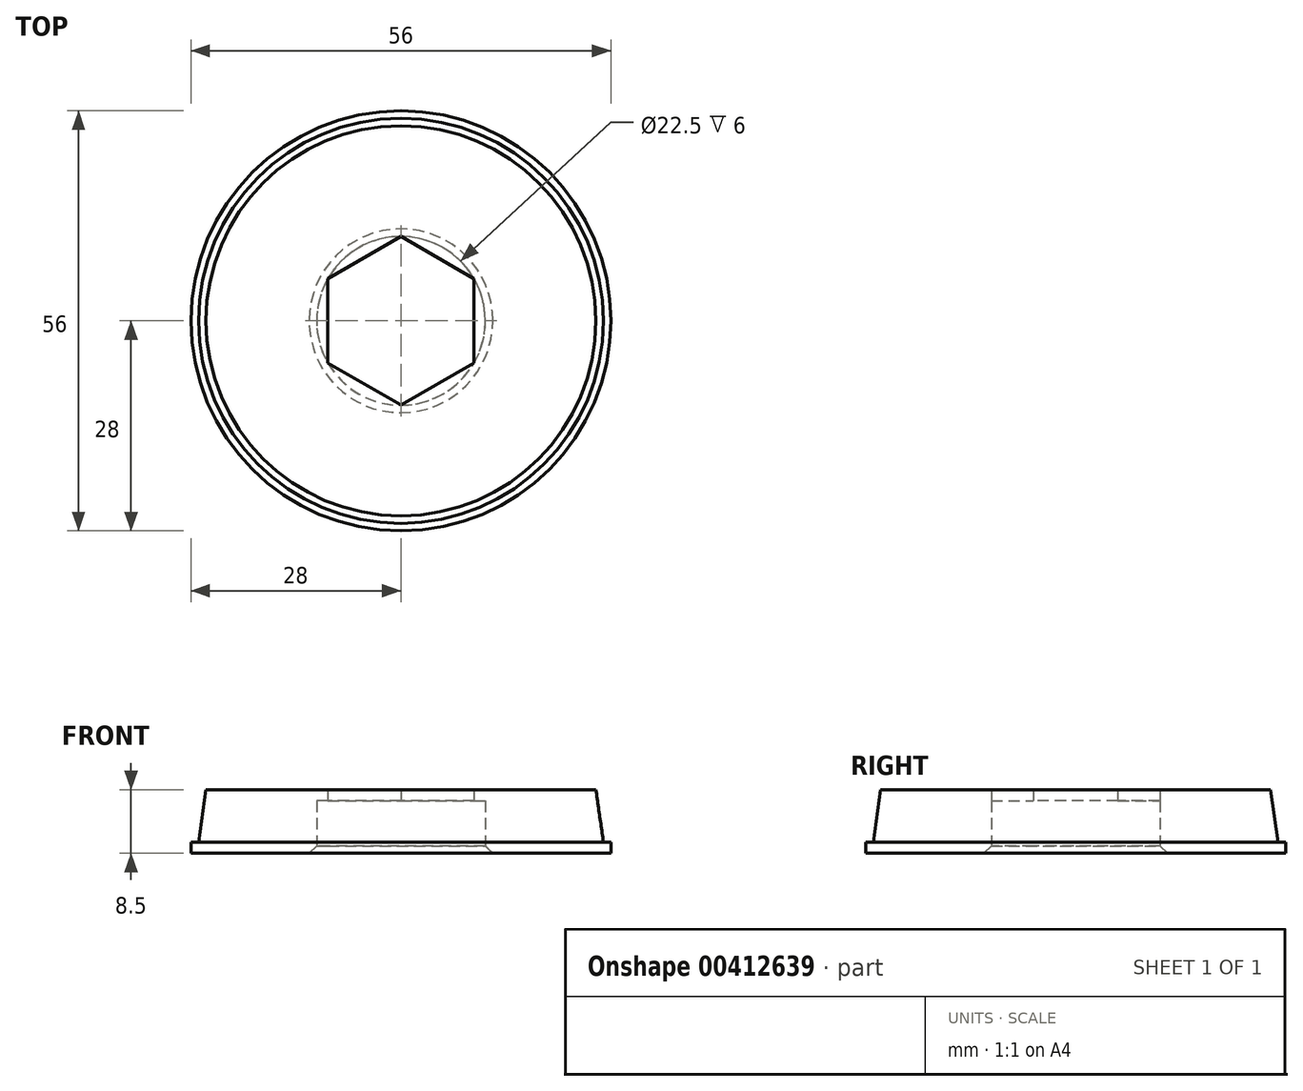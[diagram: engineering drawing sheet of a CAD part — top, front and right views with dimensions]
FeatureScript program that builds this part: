
annotation { "Feature Type Name" : "Feature", "Feature Type Description" : "" }
export const myFeature = defineFeature(function(context is Context, id is Id, definition is map)
    precondition{}
    {
        {
            assignVariable(context, id + "F0", {"name" : "BEARING_HEIGHT", "anyValue" : 7});
        }
        {
            assignVariable(context, id + "F1", {"name" : "UPPER_TICKNESS", "anyValue" : 1.5});
        }
        {
            assignVariable(context, id + "F2", {"name" : "LOWER_TICKNESS", "anyValue" : 1.5});
        }
        {
            assignVariable(context, id + "F3", {"name" : "EASY_MOUNT_CHAMFER_THING", "anyValue" : 1});
        }
        {
            assignVariable(context, id + "F4", {"name" : "BEARING_CHAMFER", "anyValue" : 1});
        }
        {
            var Q0;
            Q0=qCreatedBy(makeId("Top.planeOp"),FACE);
            var sketch = newSketch(context, id + "F5", { "sketchPlane" : qUnion([Q0])});
            skCircle(sketch, "E0", {"center": v(0, 0) * mm, "radius": 27 * mm});
            skCircle(sketch, "E1", {"center": v(0, 0) * mm, "radius": 11.25 * mm});
            skCircle(sketch, "E2", {"center": v(0, 0) * mm, "radius": 28 * mm});
            skCircle(sketch, "E3.cCircle", {"center": v(0, 0) * mm, "radius": 9.74 * mm, "construction": true});
            skLineSegment(sketch, "E3.0", {"start": v(9.74, 5.62) * mm, "end": v(9.74, -5.62) * mm});
            skLineSegment(sketch, "E3.1", {"start": v(9.74, -5.63) * mm, "end": v(0, -11.25) * mm});
            skLineSegment(sketch, "E3.2", {"start": v(0, -11.25) * mm, "end": v(-9.74, -5.62) * mm});
            skLineSegment(sketch, "E3.3", {"start": v(-9.74, -5.62) * mm, "end": v(-9.74, 5.62) * mm});
            skLineSegment(sketch, "E3.4", {"start": v(-9.74, 5.63) * mm, "end": v(0, 11.25) * mm});
            skLineSegment(sketch, "E3.5", {"start": v(0, 11.25) * mm, "end": v(9.74, 5.62) * mm});
            skPoint(sketch, "E3.0.midPoint", {"position": v(9.74, 0) * mm});
            skSolve(sketch);
        }
        {
            var Q0;
            Q0=makeQuery(id+"F5.imprint","IMPRINT",FACE,{"disambiguationData":[TD([[makeQuery(id+"F5.imprint","IMPRINT",EDGE,{"derivedFrom":sQuery(id+"F5.wireOp",EDGE,"E0")}),1.0]])]});
            var Q1;
            {var subQ0=sQuery(id+"F5.wireOp",EDGE,"E3.3");Q1=makeQuery(id+"F5.imprint","IMPRINT",FACE,{"disambiguationData":[TD([[makeQuery(id+"F5.imprint","IMPRINT",EDGE,{"derivedFrom":subQ0}),1.0]])]});}
            var Q2;
            {var subQ0=sQuery(id+"F5.wireOp",EDGE,"E3.5");Q2=makeQuery(id+"F5.imprint","IMPRINT",FACE,{"disambiguationData":[TD([[makeQuery(id+"F5.imprint","IMPRINT",EDGE,{"derivedFrom":subQ0}),1.0]])]});}
            var Q3;
            {var subQ0=sQuery(id+"F5.wireOp",EDGE,"E3.0");Q3=makeQuery(id+"F5.imprint","IMPRINT",FACE,{"disambiguationData":[TD([[makeQuery(id+"F5.imprint","IMPRINT",EDGE,{"derivedFrom":subQ0}),1.0]])]});}
            var Q4;
            {var subQ0=sQuery(id+"F5.wireOp",EDGE,"E3.1");Q4=makeQuery(id+"F5.imprint","IMPRINT",FACE,{"disambiguationData":[TD([[makeQuery(id+"F5.imprint","IMPRINT",EDGE,{"derivedFrom":subQ0}),1.0]])]});}
            var Q5;
            {var subQ0=sQuery(id+"F5.wireOp",EDGE,"E3.2");Q5=makeQuery(id+"F5.imprint","IMPRINT",FACE,{"disambiguationData":[TD([[makeQuery(id+"F5.imprint","IMPRINT",EDGE,{"derivedFrom":subQ0}),1.0]])]});}
            var Q6;
            {var subQ0=sQuery(id+"F5.wireOp",EDGE,"E3.4");Q6=makeQuery(id+"F5.imprint","IMPRINT",FACE,{"disambiguationData":[TD([[makeQuery(id+"F5.imprint","IMPRINT",EDGE,{"derivedFrom":subQ0}),1.0]])]});}
            var Q7;
            Q7=makeQuery(id+"F5.imprint","IMPRINT",FACE,{"disambiguationData":[TD([[makeQuery(id+"F5.imprint","IMPRINT",EDGE,{"derivedFrom":sQuery(id+"F5.wireOp",EDGE,"E3.0")}),-1.0]])]});
            extrude(context, id + "F6", {"entities" : qUnion([Q0, Q1, Q2, Q3, Q4, Q5, Q6, Q7]), "depth" : (getVariable(context, 'BEARING_HEIGHT') + getVariable(context, 'UPPER_TICKNESS') - getVariable(context, 'LOWER_TICKNESS')) * mm, "hasSecondDirectionDraft" : true, "secondDirectionDraftAngle" : 3 * degree});
        }
        {
            var Q0;
            Q0=makeQuery(id+"F5.imprint","IMPRINT",FACE,{"disambiguationData":[TD([[makeQuery(id+"F5.imprint","IMPRINT",EDGE,{"derivedFrom":sQuery(id+"F5.wireOp",EDGE,"E3.0")}),-1.0]])]});
            var Q1;
            Q1=makeQuery(id+"F5.imprint","IMPRINT",FACE,{"disambiguationData":[TD([[makeQuery(id+"F5.imprint","IMPRINT",EDGE,{"derivedFrom":sQuery(id+"F5.wireOp",EDGE,"E0")}),1.0]])]});
            var Q2;
            {var subQ0=sQuery(id+"F5.wireOp",EDGE,"E3.0");Q2=makeQuery(id+"F5.imprint","IMPRINT",FACE,{"disambiguationData":[TD([[makeQuery(id+"F5.imprint","IMPRINT",EDGE,{"derivedFrom":subQ0}),1.0]])]});}
            var Q3;
            {var subQ0=sQuery(id+"F5.wireOp",EDGE,"E3.1");Q3=makeQuery(id+"F5.imprint","IMPRINT",FACE,{"disambiguationData":[TD([[makeQuery(id+"F5.imprint","IMPRINT",EDGE,{"derivedFrom":subQ0}),1.0]])]});}
            var Q4;
            {var subQ0=sQuery(id+"F5.wireOp",EDGE,"E3.2");Q4=makeQuery(id+"F5.imprint","IMPRINT",FACE,{"disambiguationData":[TD([[makeQuery(id+"F5.imprint","IMPRINT",EDGE,{"derivedFrom":subQ0}),1.0]])]});}
            var Q5;
            {var subQ0=sQuery(id+"F5.wireOp",EDGE,"E3.3");Q5=makeQuery(id+"F5.imprint","IMPRINT",FACE,{"disambiguationData":[TD([[makeQuery(id+"F5.imprint","IMPRINT",EDGE,{"derivedFrom":subQ0}),1.0]])]});}
            var Q6;
            {var subQ0=sQuery(id+"F5.wireOp",EDGE,"E3.5");Q6=makeQuery(id+"F5.imprint","IMPRINT",FACE,{"disambiguationData":[TD([[makeQuery(id+"F5.imprint","IMPRINT",EDGE,{"derivedFrom":subQ0}),1.0]])]});}
            var Q7;
            {var subQ0=sQuery(id+"F5.wireOp",EDGE,"E3.4");Q7=makeQuery(id+"F5.imprint","IMPRINT",FACE,{"disambiguationData":[TD([[makeQuery(id+"F5.imprint","IMPRINT",EDGE,{"derivedFrom":subQ0}),1.0]])]});}
            var Q8;
            Q8=makeQuery(id+"F5.imprint","IMPRINT",FACE,{"disambiguationData":[TD([[makeQuery(id+"F5.imprint","IMPRINT",EDGE,{"derivedFrom":sQuery(id+"F5.wireOp",EDGE,"E0")}),-1.0]])]});
            extrude(context, id + "F7", {"entities" : qUnion([Q0, Q1, Q2, Q3, Q4, Q5, Q6, Q7, Q8]), "operationType" : NewBodyOperationType.ADD, "oppositeDirection" : true, "depth" : getVariable(context, 'LOWER_TICKNESS') * mm});
        }
        {
            var Q0;
            Q0=makeQuery(id+"F5.imprint","IMPRINT",FACE,{"disambiguationData":[TD([[makeQuery(id+"F5.imprint","IMPRINT",EDGE,{"derivedFrom":sQuery(id+"F5.wireOp",EDGE,"E3.0")}),-1.0]])]});
            var Q1;
            Q1=makeQuery(id+"F6.opExtrude","CAP_FACE",FACE,{"disambiguationData":[OSD([sQuery(id+"F5.wireOp",EDGE,"E0"),sQuery(id+"F5.wireOp",EDGE,"E1")])],"isStart":false});
            extrude(context, id + "F8", {"entities" : qUnion([Q0]), "operationType" : NewBodyOperationType.REMOVE, "endBound" : BoundingType.THROUGH_ALL, "endBoundEntityFace" : qUnion([Q1]), "depth" : 25 * mm, "hasSecondDirection" : true, "secondDirectionBound" : SecondDirectionBoundingType.THROUGH_ALL, "secondDirectionOppositeDirection" : true, "secondDirectionDepth" : 2 * mm});
        }
        {
            var Q0;
            {var subQ0=sQuery(id+"F5.wireOp",EDGE,"E3.2");Q0=makeQuery(id+"F5.imprint","IMPRINT",FACE,{"disambiguationData":[TD([[makeQuery(id+"F5.imprint","IMPRINT",EDGE,{"derivedFrom":subQ0}),1.0]])]});}
            var Q1;
            {var subQ0=sQuery(id+"F5.wireOp",EDGE,"E3.1");Q1=makeQuery(id+"F5.imprint","IMPRINT",FACE,{"disambiguationData":[TD([[makeQuery(id+"F5.imprint","IMPRINT",EDGE,{"derivedFrom":subQ0}),1.0]])]});}
            var Q2;
            {var subQ0=sQuery(id+"F5.wireOp",EDGE,"E3.0");Q2=makeQuery(id+"F5.imprint","IMPRINT",FACE,{"disambiguationData":[TD([[makeQuery(id+"F5.imprint","IMPRINT",EDGE,{"derivedFrom":subQ0}),1.0]])]});}
            var Q3;
            {var subQ0=sQuery(id+"F5.wireOp",EDGE,"E3.5");Q3=makeQuery(id+"F5.imprint","IMPRINT",FACE,{"disambiguationData":[TD([[makeQuery(id+"F5.imprint","IMPRINT",EDGE,{"derivedFrom":subQ0}),1.0]])]});}
            var Q4;
            {var subQ0=sQuery(id+"F5.wireOp",EDGE,"E3.4");Q4=makeQuery(id+"F5.imprint","IMPRINT",FACE,{"disambiguationData":[TD([[makeQuery(id+"F5.imprint","IMPRINT",EDGE,{"derivedFrom":subQ0}),1.0]])]});}
            var Q5;
            {var subQ0=sQuery(id+"F5.wireOp",EDGE,"E3.3");Q5=makeQuery(id+"F5.imprint","IMPRINT",FACE,{"disambiguationData":[TD([[makeQuery(id+"F5.imprint","IMPRINT",EDGE,{"derivedFrom":subQ0}),1.0]])]});}
            extrude(context, id + "F9", {"entities" : qUnion([Q0, Q1, Q2, Q3, Q4, Q5]), "operationType" : NewBodyOperationType.REMOVE, "depth" : (getVariable(context, 'BEARING_HEIGHT') - getVariable(context, 'LOWER_TICKNESS')) * mm, "hasSecondDirection" : true, "secondDirectionBound" : SecondDirectionBoundingType.THROUGH_ALL, "secondDirectionOppositeDirection" : true, "secondDirectionDepth" : 2 * mm});
        }
        {
            var Q0;
            Q0=makeQuery(id+"F6.opExtrude","CAP_EDGE",EDGE,{"disambiguationData":[OSD([sQuery(id+"F5.wireOp",EDGE,"E0")])],"isStart":false});
            chamfer(context, id + "F10", {"entities" : qUnion([Q0]), "chamferType" : ChamferType.TWO_OFFSETS, "width1" : getVariable(context, 'BEARING_HEIGHT') * mm, "oppositeDirection" : true, "width2" : getVariable(context, 'EASY_MOUNT_CHAMFER_THING') * mm, "tangentPropagation" : true});
        }
        {
            var Q0;
            {var subQ0=sQuery(id+"F5.wireOp",EDGE,"E3.5");var subQ1=sQuery(id+"F5.wireOp",EDGE,"E3.0");var subQ2=sQuery(id+"F5.wireOp",EDGE,"E1");var subQ3=makeQuery(id+"F5.imprint","INTERSECT",VERTEX,{"derivedFrom":[subQ2,subQ1,subQ0]});var subQ4=sQuery(id+"F5.wireOp",EDGE,"E3.1");var subQ5=makeQuery(id+"F5.imprint","INTERSECT",VERTEX,{"derivedFrom":[subQ2,subQ1,subQ4]});var subQ6=sQuery(id+"F5.wireOp",EDGE,"E3.2");var subQ7=makeQuery(id+"F5.imprint","INTERSECT",VERTEX,{"derivedFrom":[subQ2,subQ4,subQ6]});var subQ8=sQuery(id+"F5.wireOp",EDGE,"E3.3");var subQ9=makeQuery(id+"F5.imprint","INTERSECT",VERTEX,{"derivedFrom":[subQ2,subQ6,subQ8]});var subQ10=sQuery(id+"F5.wireOp",EDGE,"E3.4");var subQ11=makeQuery(id+"F5.imprint","INTERSECT",VERTEX,{"derivedFrom":[subQ2,subQ8,subQ10]});Q0=makeQuery(id+"F9.boolean.opBoolean","INTERSECT",EDGE,{"derivedFrom":[makeQuery(id+"F7.opExtrude","CAP_FACE",FACE,{"disambiguationData":[OSD([sQuery(id+"F5.wireOp",EDGE,"E2")])],"isStart":false}),makeQuery(id+"F9.opExtrude","SWEPT_FACE",FACE,{"disambiguationData":[OSD([subQ2]),TDD([makeQuery(id+"F5.imprint","IMPRINT",EDGE,{"disambiguationData":[TD([[subQ3,-1.0]])],"derivedFrom":subQ2})])]}),makeQuery(id+"F9.opExtrude","SWEPT_FACE",FACE,{"disambiguationData":[OSD([subQ2]),TDD([makeQuery(id+"F5.imprint","IMPRINT",EDGE,{"disambiguationData":[TD([[subQ11,1.0]])],"derivedFrom":subQ2})])]}),makeQuery(id+"F9.opExtrude","SWEPT_FACE",FACE,{"disambiguationData":[OSD([subQ2]),TDD([makeQuery(id+"F5.imprint","IMPRINT",EDGE,{"disambiguationData":[TD([[subQ9,1.0]])],"derivedFrom":subQ2})])]}),makeQuery(id+"F9.opExtrude","SWEPT_FACE",FACE,{"disambiguationData":[OSD([subQ2]),TDD([makeQuery(id+"F5.imprint","IMPRINT",EDGE,{"disambiguationData":[TD([[subQ7,1.0]])],"derivedFrom":subQ2})])]}),makeQuery(id+"F9.opExtrude","SWEPT_FACE",FACE,{"disambiguationData":[OSD([subQ2]),TDD([makeQuery(id+"F5.imprint","IMPRINT",EDGE,{"disambiguationData":[TD([[subQ5,1.0]])],"derivedFrom":subQ2})])]}),makeQuery(id+"F9.opExtrude","SWEPT_FACE",FACE,{"disambiguationData":[OSD([subQ2]),TDD([makeQuery(id+"F5.imprint","IMPRINT",EDGE,{"disambiguationData":[TD([[subQ3,1.0]])],"derivedFrom":subQ2})])]})]});}
            chamfer(context, id + "F11", {"entities" : qUnion([Q0]), "width" : getVariable(context, 'BEARING_CHAMFER') * mm, "tangentPropagation" : true});
        }
    });
